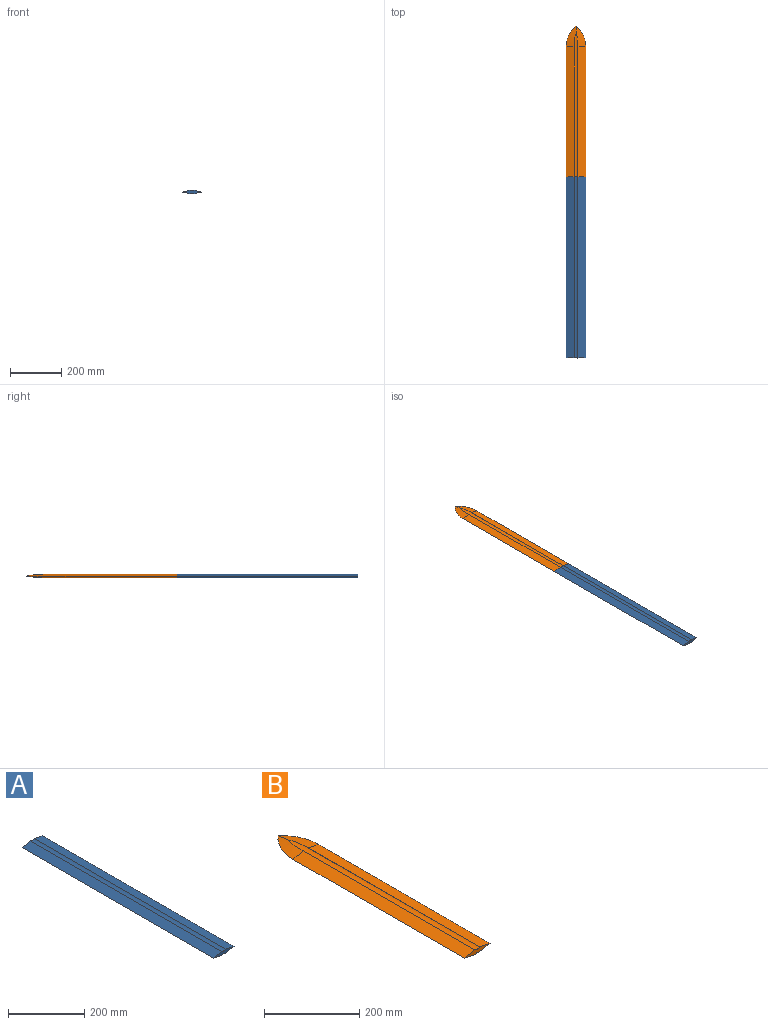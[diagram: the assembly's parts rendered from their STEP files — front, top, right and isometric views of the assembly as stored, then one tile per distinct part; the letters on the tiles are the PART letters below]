
ASSEMBLY  parts=2 mates=1
PART A: 10 faces, bbox 76.2x711.3x12.7 mm
  f0: plane 76.2x12.7mm, normal (0,-1,0), area 545.5mm2, adj f1,f2,f3,f4,f5,f6,f7,f8
  f1: plane 711.28x30.48mm, normal (0.2,0,0.98), area 22145.3mm2, adj f0,f2,f8,f9
  f2: plane 711.28x30.48mm, normal (0.2,0,-0.98), area 22145.3mm2, adj f0,f1,f7,f9
  f3: plane 711.28x30.39mm, normal (-0.2,0,0.98), area 22078.6mm2, adj f0,f4,f5,f9
  f4: plane 711.28x30.4mm, normal (-0.2,0,-0.98), area 22084.8mm2, adj f0,f3,f6,f9
  f5: cylinder r=16.18mm len=711.28mm, axis (0,-1,0), area 11349.2mm2, adj f0,f3,f8,f9
  f6: cylinder r=20.88mm len=711.28mm, axis (0,-1,0), area 11148.9mm2, adj f0,f4,f7,f9
  f7: plane 711.28x0.01mm, normal (0,0,-1), area 10.2mm2, adj f0,f2,f6,f9
  f8: plane 711.28x0.01mm, normal (0,0,1), area 10.2mm2, adj f0,f1,f5,f9
  f9: plane 76.2x12.7mm, normal (0,1,0), area 545.5mm2, adj f1,f2,f3,f4,f5,f6,f7,f8
PART B: 13 faces, bbox 76.2x589.9x12.7 mm
  f0: plane 509.4x0.01mm, normal (0,0,1), area 7.3mm2, adj f3,f7,f11,f12
  f1: plane 509.4x0.01mm, normal (0,0,-1), area 7.3mm2, adj f2,f6,f10,f12
  f2: cylinder r=20.88mm len=555.23mm, axis (0,-1,0), area 8500.8mm2, adj f1,f4,f8,f10,f12
  f3: cylinder r=16.18mm len=559.15mm, axis (0,-1,0), area 8703.3mm2, adj f0,f5,f9,f11,f12
  f4: plane 507.92x30.4mm, normal (-0.2,0,-0.98), area 15770.6mm2, adj f2,f5,f8,f12
  f5: plane 507.92x30.39mm, normal (-0.2,0,0.98), area 15766.2mm2, adj f3,f4,f9,f12
  f6: plane 507.92x30.48mm, normal (0.2,0,-0.98), area 15813.8mm2, adj f1,f7,f10,f12
  f7: plane 507.92x30.48mm, normal (0.2,0,0.98), area 15813.8mm2, adj f0,f6,f11,f12
  f8: cone r=107.22mm half-angle=78.2deg, axis (0,0,1), area 1943.2mm2, adj f2,f4,f9,f10
  f9: cone r=76.74mm half-angle=78.2deg, axis (0,0,-1), area 1916.6mm2, adj f3,f5,f8,f11
  f10: cone r=107.22mm half-angle=78.2deg, axis (0,0,1), area 1947mm2, adj f1,f2,f6,f8,f11
  f11: cone r=76.74mm half-angle=78.2deg, axis (0,0,-1), area 1921.3mm2, adj f0,f3,f7,f9,f10
  f12: plane 76.2x12.7mm, normal (0,-1,0), area 545.5mm2, adj f0,f1,f2,f3,f4,f5,f6,f7
PLACE A t=(-109.92,209.99,60.42)mm
PLACE B t=(-109.92,209.99,60.42)mm
MATE fastened B.f12 <-> A.f9  axis (0,-1,0) through (-153.38,311.59,66.72)mm
